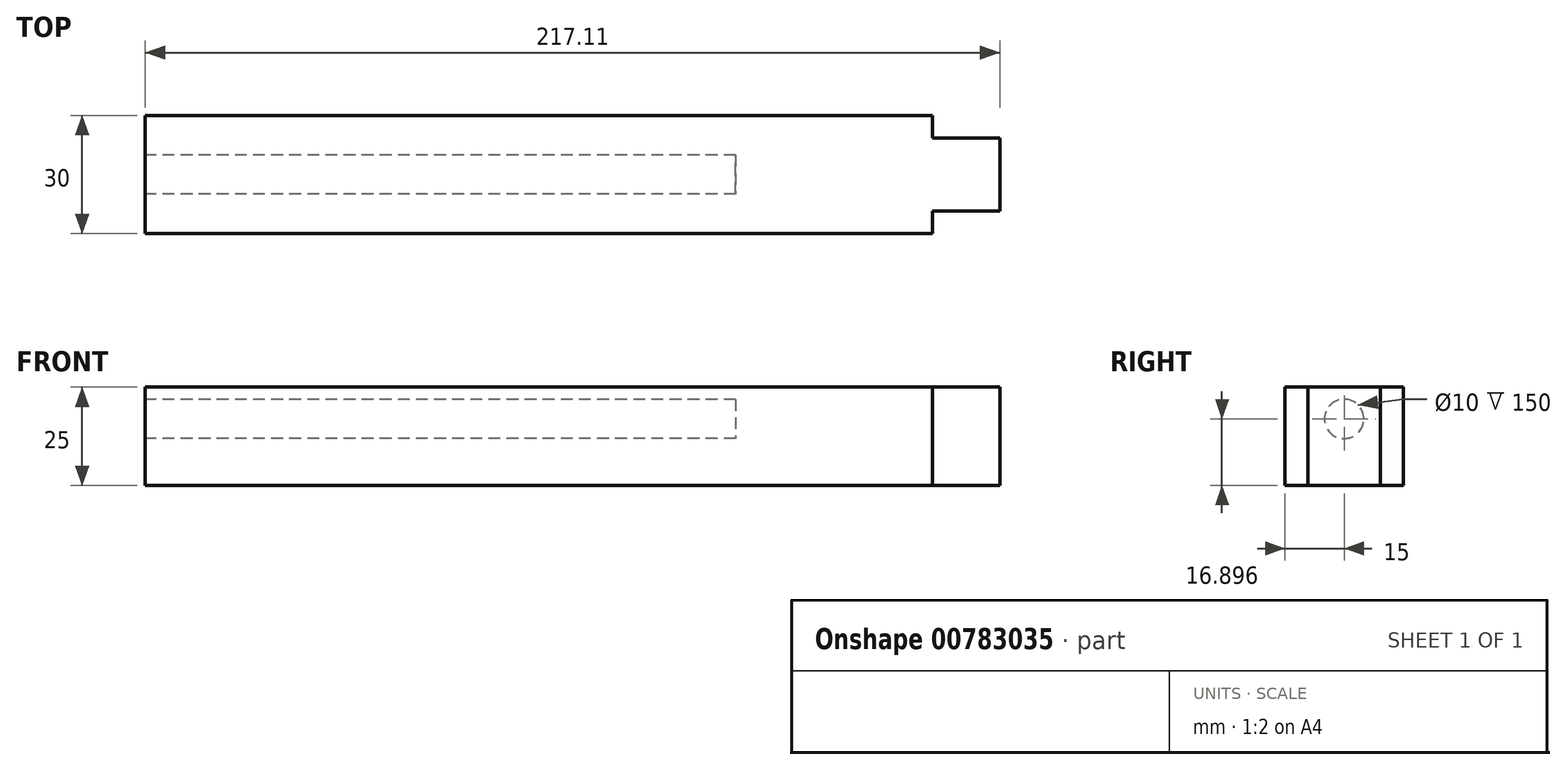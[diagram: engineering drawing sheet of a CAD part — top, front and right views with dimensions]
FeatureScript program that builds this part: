
annotation { "Feature Type Name" : "Feature", "Feature Type Description" : "" }
export const myFeature = defineFeature(function(context is Context, id is Id, definition is map)
    precondition{}
    {
        {
            var Q0;
            Q0=qCreatedBy(makeId("Top.planeOp"),FACE);
            var sketch = newSketch(context, id + "F0", { "sketchPlane" : qUnion([Q0])});
            skLineSegment(sketch, "E0.bottom", {"start": v(-99.61, 4.14) * mm, "end": v(100.39, 4.14) * mm});
            skLineSegment(sketch, "E0.top", {"start": v(-99.61, -25.86) * mm, "end": v(100.39, -25.86) * mm});
            skLineSegment(sketch, "E0.left", {"start": v(-99.61, 4.14) * mm, "end": v(-99.61, -25.86) * mm});
            skLineSegment(sketch, "E0.right", {"start": v(100.39, 4.14) * mm, "end": v(100.39, -1.64) * mm});
            skLineSegment(sketch, "E1.bottom", {"start": v(81.6, -25.86) * mm, "end": v(31.6, -25.86) * mm});
            skLineSegment(sketch, "E1.top", {"start": v(81.6, 4.14) * mm, "end": v(31.6, 4.14) * mm});
            skLineSegment(sketch, "E2.bottom", {"start": v(100.39, -1.64) * mm, "end": v(117.5, -1.64) * mm});
            skLineSegment(sketch, "E2.top", {"start": v(100.39, -20.08) * mm, "end": v(117.5, -20.08) * mm});
            skLineSegment(sketch, "E2.right", {"start": v(117.5, -1.64) * mm, "end": v(117.5, -20.08) * mm});
            skLineSegment(sketch, "E3.trimOffspring", {"start": v(100.39, -20.08) * mm, "end": v(100.39, -25.86) * mm});
            skSolve(sketch);
        }
        {
            var Q0;
            Q0 = qSketchRegion(id + "F0", true);
            extrude(context, id + "F1", {"entities" : qUnion([Q0]), "oppositeDirection" : true, "depth" : 25 * mm, "offsetDistance" : 25 * mm});
        }
        {
            var Q0;
            Q0=makeQuery(id+"F1.opExtrude","SWEPT_FACE",FACE,{"disambiguationData":[OSD([sQuery(id+"F0.wireOp",EDGE,"E0.left")])]});
            var sketch = newSketch(context, id + "F2", { "sketchPlane" : qUnion([Q0])});
            skCircle(sketch, "E4", {"center": v(10.86, -8.1) * mm, "radius": 5 * mm});
            skPoint(sketch, "E4.centerSnap0", {"position": v(10.86, -25) * mm});
            skSolve(sketch);
        }
        {
            var Q0;
            Q0=makeQuery(id+"F2.imprint","IMPRINT",FACE,{"disambiguationData":[TD([[makeQuery(id+"F2.imprint","IMPRINT",EDGE,{"derivedFrom":sQuery(id+"F2.wireOp",EDGE,"E4")}),1.0]])]});
            extrude(context, id + "F3", {"entities" : qUnion([Q0]), "operationType" : NewBodyOperationType.REMOVE, "oppositeDirection" : true, "depth" : 150 * mm, "offsetDistance" : 25 * mm});
        }
    });
